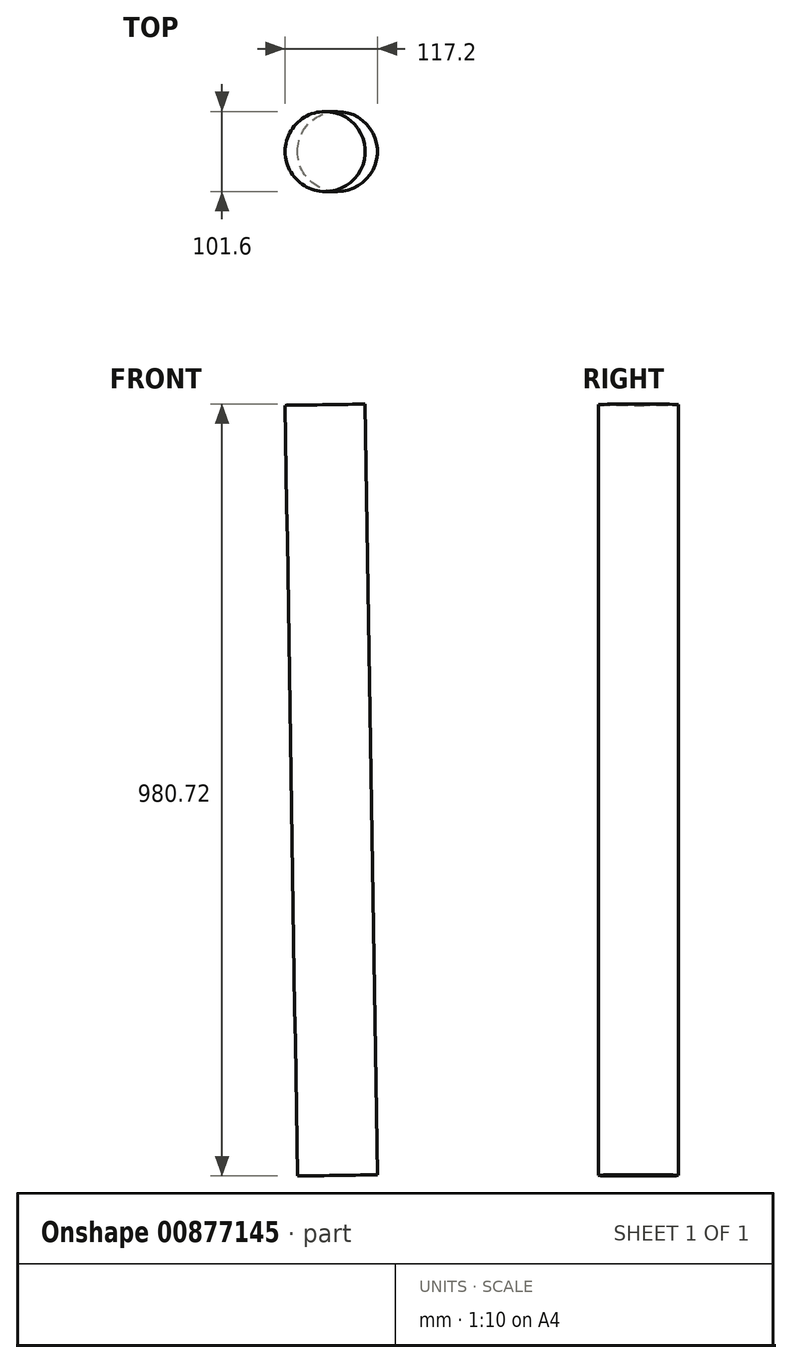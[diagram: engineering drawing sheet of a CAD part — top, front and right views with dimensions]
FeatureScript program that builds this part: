
annotation { "Feature Type Name" : "Feature", "Feature Type Description" : "" }
export const myFeature = defineFeature(function(context is Context, id is Id, definition is map)
    precondition{}
    {
        {
            var Q0;
            Q0=qCreatedBy(makeId("Front.planeOp"),FACE);
            var sketch = newSketch(context, id + "F0", { "sketchPlane" : qUnion([Q0])});
            skCircle(sketch, "E0", {"center": v(-120.6, -501.7) * mm, "radius": 120.6 * mm});
            skLineSegment(sketch, "E1", {"start": v(0, 0) * mm, "end": v(-153.67, -74.1) * mm});
            skLineSegment(sketch, "E2", {"start": v(-153.67, -74.1) * mm, "end": v(-218.92, -571.53) * mm});
            skLineSegment(sketch, "E3", {"start": v(0, 0) * mm, "end": v(135.87, 166.24) * mm});
            skLineSegment(sketch, "E4", {"start": v(136.98, 96.4) * mm, "end": v(152.6, -882.7) * mm});
            skLineSegment(sketch, "E5", {"start": v(136.98, 96.4) * mm, "end": v(135.87, 166.24) * mm});
            skCircle(sketch, "E6", {"center": v(0, 0) * mm, "radius": 31.75 * mm});
            skSolve(sketch);
        }
        {
            var Q0;
            Q0=sQuery(id+"F0.wireOp",EDGE,"E4");
            var Q1;
            Q1=qBodyType(qCreatedBy(id+"F2",EDGE),BodyType.WIRE);
            cPlane(context, id + "F1", {"entities" : qUnion([Q0, Q1]), "cplaneType" : CPlaneType.MID_PLANE, "offset" : 25 * mm, "width" : 150 * mm, "height" : 150 * mm});
        }
        {
            var Q0;
            Q0=qCreatedBy(id+"F1.planeOp",FACE);
            var sketch = newSketch(context, id + "F2", { "sketchPlane" : qUnion([Q0])});
            skCircle(sketch, "E7", {"center": v(138.5, 0) * mm, "radius": 50.8 * mm});
            skSolve(sketch);
        }
        {
            var Q0;
            Q0=makeQuery(id+"F2.imprint","IMPRINT",FACE,{"disambiguationData":[TD([[makeQuery(id+"F2.imprint","IMPRINT",EDGE,{"derivedFrom":sQuery(id+"F2.wireOp",EDGE,"E7")}),1.0]])]});
            var Q1;
            Q1=sQuery(id+"F0.wireOp",EDGE,"E4");
            sweep(context, id + "F3", {"profiles" : qUnion([Q0]), "path" : qUnion([Q1])});
        }
    });
